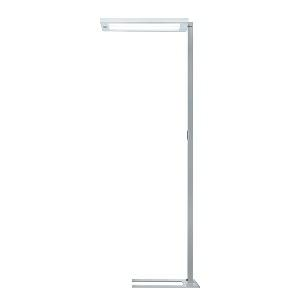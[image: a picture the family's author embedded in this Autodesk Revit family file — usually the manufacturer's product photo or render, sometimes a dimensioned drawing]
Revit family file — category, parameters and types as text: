
# Revit family: lavigo_-_dps_6000_840_r_g2_00803393_50fd
name_source: partatom
category: Lighting Fixtures
units: mm (PartAtom-declared; Revit-internal decimal feet)

## family parameters
Cut with Voids When Loaded = No
Host = Face
Light Source = No
Part Type = Normal
Room Calculation Point = No
Round Connector Dimension = Use Diameter
Shared = No

## types (1)
- LAVIGO - DPS 6000/840/R/G2 (1 x LED, 5950 lm, 4000K)
    Apparent Load = 45 VA
    Approval mark = CE
    CIE Flux Codes = 60 87 97 29 100
    Color Rendering = 80-89
    Color Temperature = 4000K
    Control Gear = Electronic ballast
    Default Elevation = 1800 mm
    Description = DPS 6000/840/R/G2|Free-standing luminaire|light source: LED|work equipment: Electronic ballast|connected load: 220-240 V, 50/60 Hz|Power consumption: approx. 45 W|standby: approx. 0,50|power factor: approx. 0,865|luminous flux: 5950 lm|luminous efficacy: 132 lm/W|light distribution: Direct/indirect|direct ratio: approx. 29 %|colour temperature: Cold white, ca. 4000 K|color rendering index (CRI): >= 80|chromaticity tolerance:  3 SDCM|technology: Presence and daylight sensor control (PIR)|operation: Multi-function switch|luminaire body|material: Steel/plastic|surface: Painted|colour: Silver metallic|lamp cover: Acrylic (PMMA), Satine|tubular section|material: Steel tube|surface: Painted|Form: Tubular section upright|colour of tubular section: Silver metallic|luminaire base|Form: C-form flat|weight (net): approx. 19.7 kg|mains lead: 3.00 m Mains plug CEE 7/VII|Fastening: Floor standing base|decorative contrast side parts: Flint grey|glare control: Prism aperture|luminance(L65): <= 3000 cd/m|unified glare rating(4H 8H): <=  16|special features: Luminaire head detachable, Cradle to Cradle Certified TM, Direct light component with edge light and light-guide technology for homogenous light exit, Flicker-free, Integrated light and presence sensor PIR, Retrofittable with TALK module, Separated, direct and indirect light individually adjustable|
    Frequency = 50 Hz
    Height = 36 mm
    Lamp = 1 x LED
    Lamp Light Flux = 5950 lm
    Lamp count = 1
    Length = 675 mm
    Luminous efficacy = 132 lm/W
    Manufacturer = Waldmann
    ModVariant = No
    Model = 00803393
    Mounting Place = Floor
    Mounting Type = Freestanding
    Number of Poles = 1
    OnlyDefault = Yes
    Power Factor = 1
    Product Name = LAVIGO - DPS 6000/840/R/G2
    Product group = Free standing luminaire
    ProductGroupID = 13
    Protection Class = Protection class I
    Protection Degree = IP 20
    RLX_Detail_Level = 1
    RLX_Emergency_Light_Flux = 0 lm
    RLX_Emergency_Type = 0
    RLX_Emergency_Type_DB = No
    RlxData = <blob elided: 37897 chars, md5=d01968c9>
    Socket = socket
    Standby Power = 0 W
    System Light Flux = 5950 lm
    System Power = 45 W
    Type Comments = Product without accessories
    Type Image = 121695000-00625713.jpg
    URL = http://relux.com
    VarID = ---
    Voltage = 230 V
    Voltage Range = 220-240 V
    Weight = 0.00 kg
    Width = 320 mm

## geometry (parser evidence)
native form markers: Blend x4, Sweep x15
no freeform markers — native parametric forms only
